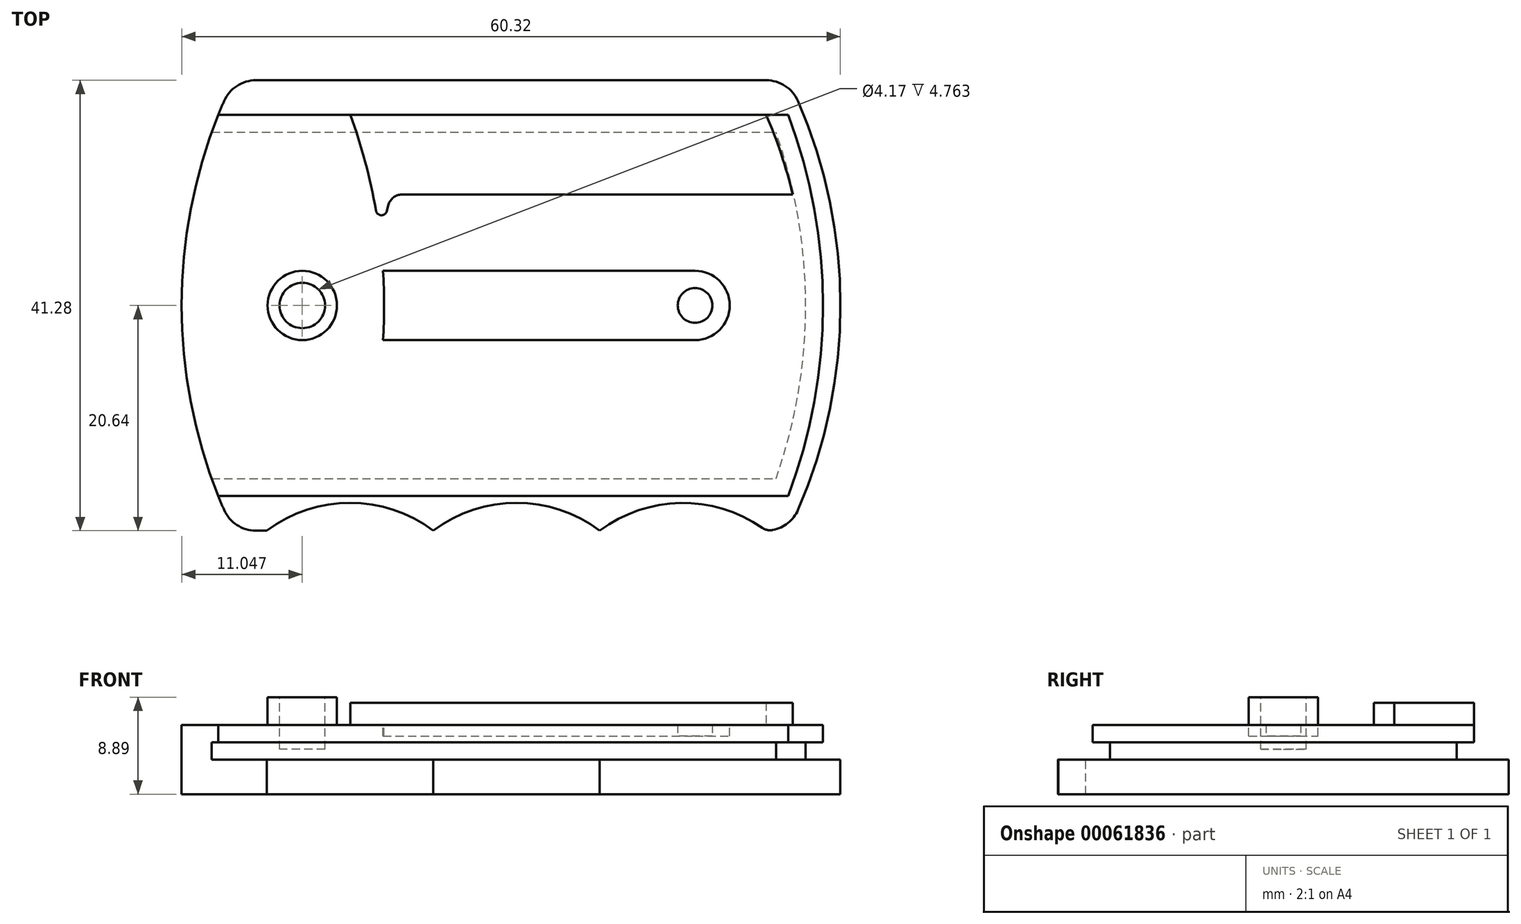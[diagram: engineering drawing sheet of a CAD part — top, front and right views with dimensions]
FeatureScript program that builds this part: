
annotation { "Feature Type Name" : "Feature", "Feature Type Description" : "" }
export const myFeature = defineFeature(function(context is Context, id is Id, definition is map)
    precondition{}
    {
        {
            var Q0;
            Q0=qCreatedBy(makeId("Top.planeOp"),FACE);
            var sketch = newSketch(context, id + "F0", { "sketchPlane" : qUnion([Q0])});
            skLineSegment(sketch, "E0.rect.bottom", {"start": v(31.75, -20.64) * mm, "end": v(-31.75, -20.64) * mm, "construction": true});
            skLineSegment(sketch, "E0.rect.top", {"start": v(31.75, 20.64) * mm, "end": v(-31.75, 20.64) * mm, "construction": true});
            skLineSegment(sketch, "E0.rect.left", {"start": v(31.75, -20.64) * mm, "end": v(31.75, 20.64) * mm, "construction": true});
            skLineSegment(sketch, "E0.rect.right", {"start": v(-31.75, -20.64) * mm, "end": v(-31.75, 20.64) * mm, "construction": true});
            skPoint(sketch, "E0.rect.middle", {"position": v(0, 0) * mm});
            skLineSegment(sketch, "E1.rect.bottom", {"start": v(25.4, 20.64) * mm, "end": v(-25.4, 20.64) * mm});
            skLineSegment(sketch, "E1.rect.top", {"start": v(25.4, -20.64) * mm, "end": v(-25.4, -20.64) * mm});
            skLineSegment(sketch, "E1.rect.left", {"start": v(25.4, 20.64) * mm, "end": v(25.4, -20.64) * mm, "construction": true});
            skLineSegment(sketch, "E1.rect.right", {"start": v(-25.4, 20.64) * mm, "end": v(-25.4, -20.64) * mm, "construction": true});
            skArc(sketch, "E2", {"start": v(-25.4, 20.64) * mm, "mid": v(-30.16, 0) * mm, "end": v(-25.4, -20.64) * mm});
            skArc(sketch, "E3", {"start": v(25.4, -20.64) * mm, "mid": v(30.16, 0) * mm, "end": v(25.4, 20.64) * mm});
            skSolve(sketch);
        }
        {
            var Q0;
            Q0=makeQuery(id+"F0.imprint","IMPRINT",FACE,{"disambiguationData":[TD([[makeQuery(id+"F0.imprint","IMPRINT",EDGE,{"derivedFrom":sQuery(id+"F0.wireOp",EDGE,"E1.rect.bottom")}),1.0]])]});
            extrude(context, id + "F1", {"entities" : qUnion([Q0]), "depth" : 6.35 * mm});
        }
        {
            var Q0;
            Q0=makeQuery(id+"F1.opExtrude","SWEPT_EDGE",EDGE,{"disambiguationData":[OSD([sQuery(id+"F0.wireOp",EDGE,"E1.rect.bottom"),sQuery(id+"F0.wireOp",EDGE,"E2")])]});
            var Q1;
            Q1=makeQuery(id+"F1.opExtrude","SWEPT_EDGE",EDGE,{"disambiguationData":[OSD([sQuery(id+"F0.wireOp",EDGE,"E1.rect.top"),sQuery(id+"F0.wireOp",EDGE,"E2")])]});
            var Q2;
            Q2=makeQuery(id+"F1.opExtrude","SWEPT_EDGE",EDGE,{"disambiguationData":[OSD([sQuery(id+"F0.wireOp",EDGE,"E1.rect.top"),sQuery(id+"F0.wireOp",EDGE,"E3")])]});
            var Q3;
            Q3=makeQuery(id+"F1.opExtrude","SWEPT_EDGE",EDGE,{"disambiguationData":[OSD([sQuery(id+"F0.wireOp",EDGE,"E1.rect.bottom"),sQuery(id+"F0.wireOp",EDGE,"E3")])]});
            fillet(context, id + "F2", {"entities" : qUnion([Q0, Q1, Q2, Q3]), "radius" : 3.17 * mm, "tangentPropagation" : true, "allowEdgeOverflow" : false});
        }
        {
            var Q0;
            Q0=makeQuery(id+"F1.opExtrude","CAP_FACE",FACE,{"disambiguationData":[OSD([sQuery(id+"F0.wireOp",EDGE,"E1.rect.bottom"),sQuery(id+"F0.wireOp",EDGE,"E1.rect.top"),sQuery(id+"F0.wireOp",EDGE,"E2"),sQuery(id+"F0.wireOp",EDGE,"E3")])],"isStart":false});
            var sketch = newSketch(context, id + "F3", { "sketchPlane" : qUnion([Q0])});
            skCircle(sketch, "E4", {"center": v(-19.11, 0) * mm, "radius": 3.18 * mm});
            skLineSegment(sketch, "E5", {"start": v(-30.16, 0) * mm, "end": v(-30.16, 7.73) * mm, "construction": true});
            skSolve(sketch);
        }
        {
            var Q0;
            Q0=makeQuery(id+"F3.imprint","IMPRINT",FACE,{"disambiguationData":[TD([[makeQuery(id+"F3.imprint","IMPRINT",EDGE,{"derivedFrom":sQuery(id+"F3.wireOp",EDGE,"E4")}),1.0]])]});
            extrude(context, id + "F4", {"entities" : qUnion([Q0]), "operationType" : NewBodyOperationType.ADD, "depth" : 2.54 * mm});
        }
        {
            var Q0;
            Q0=makeQuery(id+"F1.opExtrude","CAP_FACE",FACE,{"disambiguationData":[OSD([sQuery(id+"F0.wireOp",EDGE,"E1.rect.bottom"),sQuery(id+"F0.wireOp",EDGE,"E1.rect.top"),sQuery(id+"F0.wireOp",EDGE,"E2"),sQuery(id+"F0.wireOp",EDGE,"E3")])],"isStart":false});
            var sketch = newSketch(context, id + "F5", { "sketchPlane" : qUnion([Q0])});
            skLineSegment(sketch, "E6.0", {"start": v(21.84, 20.64) * mm, "end": v(-16, 20.64) * mm});
            skArc(sketch, "E7", {"start": v(-12.02, 6.35) * mm, "mid": v(-13.49, 13.64) * mm, "end": v(-16, 20.64) * mm});
            skArc(sketch, "E8", {"start": v(-10, 10.16) * mm, "mid": v(-10.76, 9.9) * mm, "end": v(-11.22, 9.23) * mm});
            skLineSegment(sketch, "E9", {"start": v(-10, 10.16) * mm, "end": v(25.8, 10.16) * mm});
            skPoint(sketch, "E10.orphan", {"position": v(-23.37, 20.64) * mm});
            skPoint(sketch, "E11.orphan", {"position": v(23.37, 20.64) * mm});
            skLineSegment(sketch, "E12", {"start": v(-11.22, 9.23) * mm, "end": v(-12.02, 6.35) * mm});
            skLineSegment(sketch, "E13", {"start": v(-12.02, 6.35) * mm, "end": v(-12.02, 8.35) * mm, "construction": true});
            skLineSegment(sketch, "E14", {"start": v(-16, 20.64) * mm, "end": v(-12.02, 6.35) * mm, "construction": true});
            skPoint(sketch, "E15.orphan", {"position": v(26.28, -18.72) * mm});
            skLineSegment(sketch, "E16.0", {"start": v(23.38, 17.14) * mm, "end": v(23.38, 17.14) * mm});
            skArc(sketch, "E17.0", {"start": v(25.8, 10.16) * mm, "mid": v(24.15, 15.53) * mm, "end": v(21.84, 20.64) * mm});
            skLineSegment(sketch, "E18", {"start": v(-16.93, 0) * mm, "end": v(-72.04, 0) * mm, "construction": true});
            skSolve(sketch);
        }
        {
            var Q0;
            Q0=makeQuery(id+"F5.imprint","IMPRINT",FACE,{"disambiguationData":[TD([[makeQuery(id+"F5.imprint","IMPRINT",EDGE,{"derivedFrom":sQuery(id+"F5.wireOp",EDGE,"E6.0")}),1.0]])]});
            extrude(context, id + "F6", {"entities" : qUnion([Q0]), "operationType" : NewBodyOperationType.ADD, "depth" : 2.03 * mm});
        }
        {
            var Q0;
            Q0=makeQuery(id+"F6.opExtrude","SWEPT_EDGE",EDGE,{"disambiguationData":[OSD([sQuery(id+"F5.wireOp",EDGE,"E7"),sQuery(id+"F5.wireOp",EDGE,"E12")])]});
            fillet(context, id + "F7", {"entities" : qUnion([Q0]), "radius" : 0.5 * mm, "tangentPropagation" : true, "allowEdgeOverflow" : false});
        }
        {
            var Q0;
            Q0=makeQuery(id+"F6.opExtrude","SWEPT_EDGE",EDGE,{"disambiguationData":[OSD([sQuery(id+"F0.wireOp",EDGE,"E1.rect.bottom"),sQuery(id+"F5.wireOp",EDGE,"E6.0"),sQuery(id+"F5.wireOp",EDGE,"E17.0")])]});
            fillet(context, id + "F8", {"entities" : qUnion([Q0]), "radius" : 3.17 * mm, "tangentPropagation" : true, "allowEdgeOverflow" : false});
        }
        {
            var Q0;
            Q0=makeQuery(id+"F4.opExtrude","CAP_FACE",FACE,{"disambiguationData":[OSD([sQuery(id+"F3.wireOp",EDGE,"E4")])],"isStart":false});
            var sketch = newSketch(context, id + "F9", { "sketchPlane" : qUnion([Q0])});
            skCircle(sketch, "E19", {"center": v(-19.11, 0) * mm, "radius": 2.08 * mm});
            skSolve(sketch);
        }
        {
            var Q0;
            Q0=makeQuery(id+"F9.imprint","IMPRINT",FACE,{"disambiguationData":[TD([[makeQuery(id+"F9.imprint","IMPRINT",EDGE,{"derivedFrom":sQuery(id+"F9.wireOp",EDGE,"E19")}),1.0]])]});
            extrude(context, id + "F10", {"entities" : qUnion([Q0]), "operationType" : NewBodyOperationType.REMOVE, "oppositeDirection" : true, "depth" : 4.76 * mm});
        }
        {
            var Q0;
            Q0=makeQuery(id+"F1.opExtrude","CAP_FACE",FACE,{"disambiguationData":[OSD([sQuery(id+"F0.wireOp",EDGE,"E1.rect.bottom"),sQuery(id+"F0.wireOp",EDGE,"E1.rect.top"),sQuery(id+"F0.wireOp",EDGE,"E2"),sQuery(id+"F0.wireOp",EDGE,"E3")])],"isStart":false});
            var sketch = newSketch(context, id + "F11", { "sketchPlane" : qUnion([Q0])});
            skLineSegment(sketch, "E20", {"start": v(-19.11, 0) * mm, "end": v(16.93, 0) * mm, "construction": true});
            skArc(sketch, "E21.0", {"start": v(-11.72, -3.18) * mm, "mid": v(-11.62, 0) * mm, "end": v(-11.72, 3.18) * mm});
            skPoint(sketch, "E22.orphan", {"position": v(-12.37, 8.7) * mm});
            skLineSegment(sketch, "E23.0", {"start": v(23.37, -20.64) * mm, "end": v(-23.37, -20.64) * mm, "construction": true});
            skLineSegment(sketch, "E24.rect.bottom", {"start": v(-11.72, -3.18) * mm, "end": v(20.03, -3.18) * mm});
            skLineSegment(sketch, "E24.rect.top", {"start": v(-11.72, 3.18) * mm, "end": v(20.03, 3.18) * mm});
            skLineSegment(sketch, "E24.rect.right", {"start": v(20.03, -3.17) * mm, "end": v(20.03, 3.18) * mm});
            skPoint(sketch, "E24.rect.middle", {"position": v(-4.35, 0) * mm});
            skPoint(sketch, "E25.orphan", {"position": v(-28.74, 3.18) * mm});
            skPoint(sketch, "E26.orphan", {"position": v(-28.74, -3.18) * mm});
            skPoint(sketch, "E27.trimOffspring.end.orphan", {"position": v(-16, 20.64) * mm});
            skSolve(sketch);
        }
        {
            var Q0;
            Q0=qSketchRegion(id+"F11",true);
            extrude(context, id + "F12", {"entities" : qUnion([Q0]), "operationType" : NewBodyOperationType.REMOVE, "oppositeDirection" : true, "depth" : 1.02 * mm});
        }
        {
            var Q0;
            Q0=makeQuery(id+"F12.boolean.opBoolean","COPY",EDGE,{"derivedFrom":makeQuery(id+"F12.opExtrude","SWEPT_EDGE",EDGE,{"disambiguationData":[OSD([sQuery(id+"F11.wireOp",EDGE,"E24.rect.top"),sQuery(id+"F11.wireOp",EDGE,"E24.rect.right")])]})});
            var Q1;
            Q1=makeQuery(id+"F12.boolean.opBoolean","COPY",EDGE,{"derivedFrom":makeQuery(id+"F12.opExtrude","SWEPT_EDGE",EDGE,{"disambiguationData":[OSD([sQuery(id+"F11.wireOp",EDGE,"E24.rect.bottom"),sQuery(id+"F11.wireOp",EDGE,"E24.rect.right")])]})});
            fillet(context, id + "F13", {"entities" : qUnion([Q0, Q1]), "radius" : 3.17 * mm, "tangentPropagation" : true, "allowEdgeOverflow" : false});
        }
        {
            var Q0;
            Q0=makeQuery(id+"F12.boolean.opBoolean","COPY",FACE,{"derivedFrom":makeQuery(id+"F12.opExtrude","CAP_FACE",FACE,{"disambiguationData":[OSD([sQuery(id+"F11.wireOp",EDGE,"E21.0"),sQuery(id+"F11.wireOp",EDGE,"E24.rect.bottom"),sQuery(id+"F11.wireOp",EDGE,"E24.rect.top"),sQuery(id+"F11.wireOp",EDGE,"E24.rect.right")])],"isStart":false})});
            var sketch = newSketch(context, id + "F14", { "sketchPlane" : qUnion([Q0])});
            skCircle(sketch, "E28", {"center": v(16.85, 0) * mm, "radius": 1.59 * mm});
            skSolve(sketch);
        }
        {
            var Q0;
            Q0=qSketchRegion(id+"F14",true);
            var Q1;
            Q1=makeQuery(id+"F1.opExtrude","CAP_FACE",FACE,{"disambiguationData":[OSD([sQuery(id+"F0.wireOp",EDGE,"E1.rect.bottom"),sQuery(id+"F0.wireOp",EDGE,"E1.rect.top"),sQuery(id+"F0.wireOp",EDGE,"E2"),sQuery(id+"F0.wireOp",EDGE,"E3")])],"isStart":false});
            extrude(context, id + "F15", {"entities" : qUnion([Q0]), "operationType" : NewBodyOperationType.ADD, "endBound" : BoundingType.UP_TO_SURFACE, "endBoundEntityFace" : qUnion([Q1]), "depth" : 2.03 * mm});
        }
        {
            var Q0;
            Q0=makeQuery(id+"F1.opExtrude","CAP_FACE",FACE,{"disambiguationData":[OSD([sQuery(id+"F0.wireOp",EDGE,"E1.rect.bottom"),sQuery(id+"F0.wireOp",EDGE,"E1.rect.top"),sQuery(id+"F0.wireOp",EDGE,"E2"),sQuery(id+"F0.wireOp",EDGE,"E3")])],"isStart":false});
            var sketch = newSketch(context, id + "F16", { "sketchPlane" : qUnion([Q0])});
            skArc(sketch, "E29", {"start": v(-25.3, 14.94) * mm, "mid": v(-19.58, 13.58) * mm, "end": v(-13.87, 14.94) * mm});
            skLineSegment(sketch, "E30", {"start": v(-25.3, 14.94) * mm, "end": v(-13.87, 14.94) * mm, "construction": true});
            skArc(sketch, "E31.0", {"start": v(-13.87, 14.94) * mm, "mid": v(-14.85, 17.82) * mm, "end": v(-16, 20.64) * mm});
            skPoint(sketch, "E32.orphan", {"position": v(-12.37, 8.7) * mm});
            skLineSegment(sketch, "E33", {"start": v(-25.3, 14.94) * mm, "end": v(-25.3, 20.77) * mm});
            skLineSegment(sketch, "E34", {"start": v(-25.3, 20.77) * mm, "end": v(-16, 20.64) * mm});
            skSolve(sketch);
        }
        {
            var Q0;
            {var subQ0=sQuery(id+"F0.wireOp",EDGE,"E1.rect.bottom");Q0=makeQuery(id+"FU7PWPYbLKA2UAa_1.boolean.opBoolean","MERGE",EDGE,{"derivedFrom":[makeQuery(id+"F6.opExtrude","SWEPT_EDGE",EDGE,{"disambiguationData":[OSD([subQ0,sQuery(id+"F5.wireOp",EDGE,"E6.0"),sQuery(id+"F5.wireOp",EDGE,"E7")])]}),makeQuery(id+"FU7PWPYbLKA2UAa_1.opExtrude","SWEPT_EDGE",EDGE,{"disambiguationData":[OSD([subQ0,sQuery(id+"F16.wireOp",EDGE,"E31.0"),sQuery(id+"F16.wireOp",EDGE,"E34")])]})]});}
            fillet(context, id + "F17", {"entities" : qUnion([Q0]), "radius" : 0.8 * mm, "tangentPropagation" : true, "allowEdgeOverflow" : false});
        }
        {
            var Q0;
            Q0=makeQuery(id+"F1.opExtrude","CAP_FACE",FACE,{"disambiguationData":[OSD([sQuery(id+"F0.wireOp",EDGE,"E1.rect.bottom"),sQuery(id+"F0.wireOp",EDGE,"E1.rect.top"),sQuery(id+"F0.wireOp",EDGE,"E2"),sQuery(id+"F0.wireOp",EDGE,"E3")])],"isStart":false});
            var sketch = newSketch(context, id + "F18", { "sketchPlane" : qUnion([Q0])});
            skLineSegment(sketch, "E35.0", {"start": v(23.37, -20.64) * mm, "end": v(-7.11, -20.64) * mm});
            skArc(sketch, "E36", {"start": v(8.13, -20.64) * mm, "mid": v(0.5, -18.1) * mm, "end": v(-7.11, -20.64) * mm});
            skArc(sketch, "E37", {"start": v(23.37, -20.64) * mm, "mid": v(15.75, -18.1) * mm, "end": v(8.13, -20.64) * mm});
            skPoint(sketch, "E38.orphan", {"position": v(23.37, -20.64) * mm});
            skLineSegment(sketch, "E39", {"start": v(0.5, -18.1) * mm, "end": v(15.75, -18.1) * mm, "construction": true});
            skArc(sketch, "E40", {"start": v(-7.11, -20.64) * mm, "mid": v(-14.73, -18.1) * mm, "end": v(-22.35, -20.64) * mm});
            skLineSegment(sketch, "E41", {"start": v(0.5, -18.1) * mm, "end": v(-20.32, -18.1) * mm, "construction": true});
            skSolve(sketch);
        }
        {
            var Q0;
            {var subQ0=sQuery(id+"F18.wireOp",EDGE,"E37");var subQ1=makeQuery(id+"F1.opExtrude","CAP_EDGE",EDGE,{"disambiguationData":[OSD([sQuery(id+"F0.wireOp",EDGE,"E1.rect.top")])],"isStart":false});var subQ2=makeQuery(id+"F18.imprint","INTERSECT",VERTEX,{"disambiguationData":[OD(0.0)],"derivedFrom":[subQ1,subQ0]});Q0=makeQuery(id+"F18.imprint","IMPRINT",FACE,{"disambiguationData":[TD([[makeQuery(id+"F18.imprint","IMPRINT",EDGE,{"disambiguationData":[TD([[subQ2,-1.0]])],"derivedFrom":subQ0}),1.0]])]});}
            var Q1;
            {var subQ0=sQuery(id+"F18.wireOp",EDGE,"E36");var subQ1=makeQuery(id+"F1.opExtrude","CAP_EDGE",EDGE,{"disambiguationData":[OSD([sQuery(id+"F0.wireOp",EDGE,"E1.rect.top")])],"isStart":false});var subQ2=makeQuery(id+"F18.imprint","INTERSECT",VERTEX,{"disambiguationData":[OD(0.0)],"derivedFrom":[subQ1,subQ0]});Q1=makeQuery(id+"F18.imprint","IMPRINT",FACE,{"disambiguationData":[TD([[makeQuery(id+"F18.imprint","IMPRINT",EDGE,{"disambiguationData":[TD([[subQ2,1.0]])],"derivedFrom":subQ0}),1.0]])]});}
            var Q2;
            {var subQ0=sQuery(id+"F18.wireOp",EDGE,"E40");Q2=makeQuery(id+"F18.imprint","IMPRINT",FACE,{"disambiguationData":[TD([[makeQuery(id+"F18.imprint","IMPRINT",EDGE,{"derivedFrom":subQ0}),1.0]])]});}
            extrude(context, id + "F19", {"entities" : qUnion([Q0, Q1, Q2]), "operationType" : NewBodyOperationType.REMOVE, "endBound" : BoundingType.THROUGH_ALL, "oppositeDirection" : true, "depth" : 25.4 * mm});
        }
        {
            var Q0;
            {var subQ0=sQuery(id+"F18.wireOp",EDGE,"E40");var subQ1=sQuery(id+"F0.wireOp",EDGE,"E1.rect.top");var subQ2=sQuery(id+"F18.wireOp",EDGE,"E36");var subQ3=sQuery(id+"F18.wireOp",EDGE,"E35.0");Q0=makeQuery(id+"F19.boolean.opBoolean","TWEAK_EDGE",EDGE,{"derivedFrom":[makeQuery(id+"F19.opExtrude","SWEPT_EDGE",EDGE,{"disambiguationData":[OSD([subQ1,subQ3,subQ2,subQ0]),ownerDisambiguation([makeQuery(id+"F19.opExtrude","SWEPT_BODY",BODY,{"disambiguationData":[OSD([subQ3,subQ2])]})])]}),makeQuery(id+"F19.opExtrude","SWEPT_EDGE",EDGE,{"disambiguationData":[OSD([subQ1,subQ3,subQ2,subQ0]),ownerDisambiguation([makeQuery(id+"F19.opExtrude","SWEPT_BODY",BODY,{"disambiguationData":[OSD([subQ1,subQ0])]})])]})]});}
            var Q1;
            Q1=makeQuery(id+"F19.boolean.opBoolean","COPY",EDGE,{"derivedFrom":makeQuery(id+"F19.opExtrude","SWEPT_EDGE",EDGE,{"disambiguationData":[OSD([sQuery(id+"F0.wireOp",EDGE,"E1.rect.top"),sQuery(id+"F18.wireOp",EDGE,"E40")])]})});
            var Q2;
            {var subQ0=sQuery(id+"F18.wireOp",EDGE,"E36");var subQ1=sQuery(id+"F18.wireOp",EDGE,"E35.0");var subQ2=sQuery(id+"F18.wireOp",EDGE,"E37");Q2=makeQuery(id+"F19.boolean.opBoolean","TWEAK_EDGE",EDGE,{"derivedFrom":[makeQuery(id+"F19.opExtrude","SWEPT_EDGE",EDGE,{"disambiguationData":[OSD([subQ1,subQ0,subQ2]),ownerDisambiguation([makeQuery(id+"F19.opExtrude","SWEPT_BODY",BODY,{"disambiguationData":[OSD([subQ1,subQ2])]})])]}),makeQuery(id+"F19.opExtrude","SWEPT_EDGE",EDGE,{"disambiguationData":[OSD([subQ1,subQ0,subQ2]),ownerDisambiguation([makeQuery(id+"F19.opExtrude","SWEPT_BODY",BODY,{"disambiguationData":[OSD([subQ1,subQ0])]})])]})]});}
            var Q3;
            {var subQ0=sQuery(id+"F0.wireOp",EDGE,"E3");var subQ1=sQuery(id+"F0.wireOp",EDGE,"E1.rect.top");Q3=makeQuery(id+"F19.boolean.opBoolean","MERGE",EDGE,{"derivedFrom":[makeQuery(id+"F2.opFillet","BLEND_EDGE",EDGE,{"blendedFrom":[makeQuery(id+"F1.opExtrude","SWEPT_EDGE",EDGE,{"disambiguationData":[OSD([subQ1,subQ0])]}),makeQuery(id+"F1.opExtrude","SWEPT_FACE",FACE,{"disambiguationData":[OSD([subQ1])]})],"blendedInto":[makeQuery(id+"F1.opExtrude","SWEPT_FACE",FACE,{"disambiguationData":[OSD([subQ1])]})]}),makeQuery(id+"F19.opExtrude","SWEPT_EDGE",EDGE,{"disambiguationData":[OSD([sQuery(id+"F0.wireOp",EDGE,"E1.rect.bottom"),subQ1,sQuery(id+"F0.wireOp",EDGE,"E2"),subQ0,sQuery(id+"F18.wireOp",EDGE,"E35.0"),sQuery(id+"F18.wireOp",EDGE,"E37")])]})]});}
            fillet(context, id + "F20", {"entities" : qUnion([Q0, Q1, Q2, Q3]), "radius" : 1.27 * mm, "tangentPropagation" : true, "allowEdgeOverflow" : false});
        }
        {
            var Q0;
            Q0=qCreatedBy(makeId("Front.planeOp"),FACE);
            var sketch = newSketch(context, id + "F21", { "sketchPlane" : qUnion([Q0])});
            skLineSegment(sketch, "E42", {"start": v(-30.16, 0) * mm, "end": v(-30.16, 6.35) * mm, "construction": true});
            skLineSegment(sketch, "E43", {"start": v(-30.16, 3.18) * mm, "end": v(-26.99, 3.18) * mm, "construction": true});
            skLineSegment(sketch, "E44", {"start": v(-26.99, 3.18) * mm, "end": v(-26.99, 4.76) * mm, "construction": true});
            skLineSegment(sketch, "E45", {"start": v(-26.99, 4.76) * mm, "end": v(-28.58, 4.76) * mm, "construction": true});
            skLineSegment(sketch, "E46", {"start": v(-28.58, 4.76) * mm, "end": v(-28.58, 6.35) * mm, "construction": true});
            skLineSegment(sketch, "E47.0", {"start": v(-30.16, 6.35) * mm, "end": v(-28.58, 6.35) * mm, "construction": true});
            skPoint(sketch, "E48.orphan", {"position": v(-26.28, 6.35) * mm});
            skLineSegment(sketch, "E49.MirrorCS", {"start": v(26.99, 3.18) * mm, "end": v(26.99, 4.76) * mm});
            skLineSegment(sketch, "E50.MirrorCS", {"start": v(30.16, 6.35) * mm, "end": v(28.58, 6.35) * mm});
            skLineSegment(sketch, "E51.MirrorCS", {"start": v(28.58, 4.76) * mm, "end": v(28.58, 6.35) * mm});
            skLineSegment(sketch, "E52.MirrorCS", {"start": v(26.99, 4.76) * mm, "end": v(28.58, 4.76) * mm});
            skLineSegment(sketch, "E53.MirrorCS", {"start": v(30.16, 3.18) * mm, "end": v(26.99, 3.18) * mm});
            skPoint(sketch, "E54.MirrorP", {"position": v(26.28, 6.35) * mm});
            skLineSegment(sketch, "E55.MirrorCS", {"start": v(30.16, 0) * mm, "end": v(30.16, 6.35) * mm});
            skLineSegment(sketch, "E56", {"start": v(-20.64, -16.64) * mm, "end": v(-20.64, 34.21) * mm, "construction": true});
            skSolve(sketch);
        }
        {
            var Q0;
            Q0=qCreatedBy(makeId("Top.planeOp"),FACE);
            cPlane(context, id + "F22", {"entities" : qUnion([Q0]), "cplaneType" : CPlaneType.OFFSET, "offset" : 25.4 * mm, "width" : 152.4 * mm, "height" : 152.4 * mm});
        }
        {
            var Q0;
            Q0 = qSketchRegion(id + "F21", true);
            var Q1;
            Q1=sQuery(id+"F21.wireOp",EDGE,"E56");
            revolve(context, id + "F23", {"operationType" : NewBodyOperationType.REMOVE, "entities" : qUnion([Q0]), "axis" : qUnion([Q1]), "revolveType" : RevolveType.FULL, "oppositeDirection" : true});
        }
        {
            var Q0;
            Q0=qCreatedBy(makeId("Right.planeOp"),FACE);
            var sketch = newSketch(context, id + "F24", { "sketchPlane" : qUnion([Q0])});
            skLineSegment(sketch, "E57.0", {"start": v(18.72, 3.18) * mm, "end": v(20.64, 3.18) * mm, "construction": true});
            skLineSegment(sketch, "E58.0", {"start": v(17.46, 8.38) * mm, "end": v(20.64, 8.38) * mm, "construction": true});
            skLineSegment(sketch, "E59", {"start": v(20.64, 3.18) * mm, "end": v(20.64, 8.38) * mm});
            skLineSegment(sketch, "E60", {"start": v(20.64, 8.38) * mm, "end": v(17.46, 8.38) * mm});
            skLineSegment(sketch, "E61", {"start": v(17.46, 8.38) * mm, "end": v(17.46, 4.76) * mm});
            skLineSegment(sketch, "E62", {"start": v(17.46, 4.76) * mm, "end": v(15.87, 4.76) * mm});
            skLineSegment(sketch, "E63", {"start": v(15.87, 4.76) * mm, "end": v(15.87, 3.17) * mm});
            skLineSegment(sketch, "E64", {"start": v(20.64, 3.18) * mm, "end": v(15.87, 3.18) * mm});
            skLineSegment(sketch, "E65.MirrorCS", {"start": v(-18.72, 3.18) * mm, "end": v(-20.64, 3.18) * mm, "construction": true});
            skLineSegment(sketch, "E66.MirrorCS", {"start": v(-17.46, 4.76) * mm, "end": v(-15.87, 4.76) * mm});
            skLineSegment(sketch, "E67.MirrorCS", {"start": v(-20.64, 3.18) * mm, "end": v(-15.87, 3.18) * mm});
            skLineSegment(sketch, "E68.MirrorCS", {"start": v(-15.87, 4.76) * mm, "end": v(-15.87, 3.17) * mm});
            skLineSegment(sketch, "E69.MirrorCS", {"start": v(-17.46, 8.38) * mm, "end": v(-20.64, 8.38) * mm, "construction": true});
            skLineSegment(sketch, "E70.MirrorCS", {"start": v(-20.64, 8.38) * mm, "end": v(-17.46, 8.38) * mm});
            skLineSegment(sketch, "E71.MirrorCS", {"start": v(-17.46, 8.38) * mm, "end": v(-17.46, 4.76) * mm});
            skLineSegment(sketch, "E72.MirrorCS", {"start": v(-20.64, 3.18) * mm, "end": v(-20.64, 8.38) * mm});
            skPoint(sketch, "E73.orphan", {"position": v(-18.82, 8.38) * mm});
            skPoint(sketch, "E74.orphan", {"position": v(18.82, 8.38) * mm});
            skSolve(sketch);
        }
        {
            var Q0;
            Q0 = qSketchRegion(id + "F24", true);
            extrude(context, id + "F25", {"entities" : qUnion([Q0]), "operationType" : NewBodyOperationType.REMOVE, "oppositeDirection" : true, "depth" : 127 * mm, "symmetric" : true});
        }
    });
